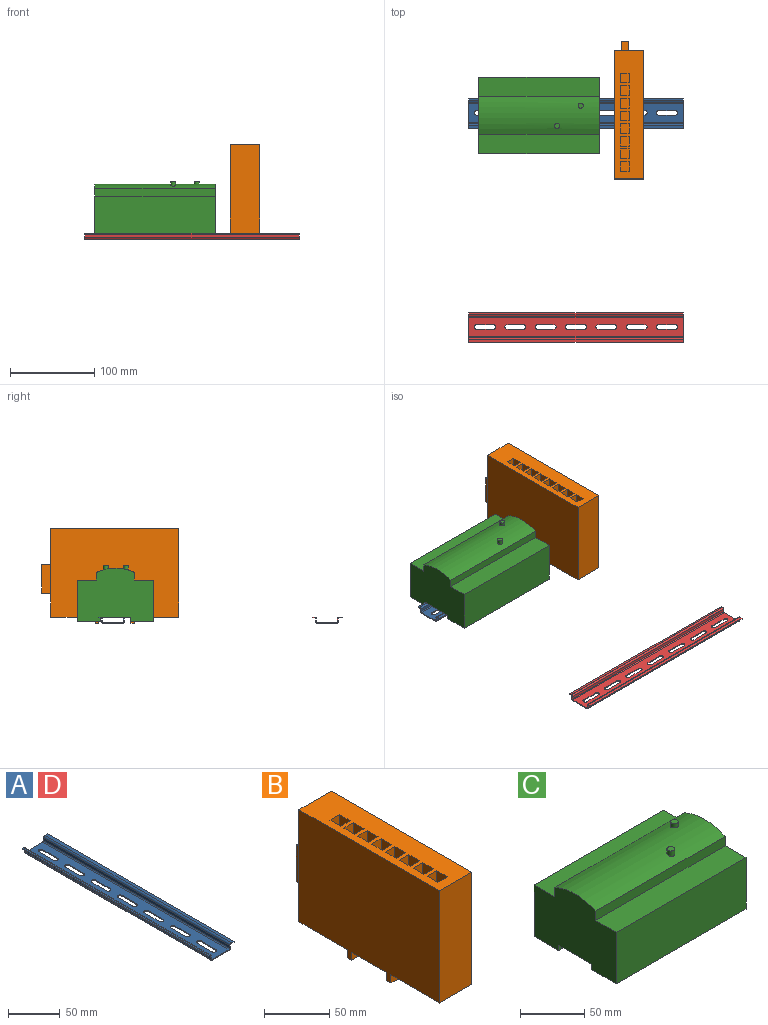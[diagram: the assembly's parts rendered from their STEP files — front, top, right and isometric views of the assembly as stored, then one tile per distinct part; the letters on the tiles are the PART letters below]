
ASSEMBLY  parts=4 mates=4
PART A: 50 faces, bbox 35x254x7.5 mm
  f0: cylinder r=1mm len=254mm, axis (0,1,0), area 399.3mm2, adj f1,f19,f20,f21
  f1: plane 254x3.5mm, normal (1,0,0), area 889mm2, adj f0,f2,f20,f21
  f2: cylinder r=2mm len=254mm, axis (0,1,0), area 797.6mm2, adj f1,f3,f20,f21
  f3: plane 254x2.19mm, normal (0,0,1), area 556.3mm2, adj f2,f4,f20,f21
  f4: plane 254x1mm, normal (-1,0,0), area 254.2mm2, adj f3,f5,f20,f21
  f5: plane 254x2.17mm, normal (0,0,-1), area 551.7mm2, adj f4,f6,f20,f21
  f6: cylinder r=1mm len=254mm, axis (0,1,0), area 399.3mm2, adj f5,f7,f20,f21
  f7: plane 254x3.5mm, normal (-1,0,0), area 889mm2, adj f6,f8,f20,f21
  f8: cylinder r=2mm len=254mm, axis (0,1,0), area 797.6mm2, adj f7,f9,f20,f21
  f9: plane 254x23mm, normal (0,0,-1), area 4973.3mm2, adj f8,f10,f20,f21,f22,f23,f24,f25
  f10: cylinder r=2mm len=254mm, axis (0,1,0), area 797.6mm2, adj f9,f11,f20,f21
  f11: plane 254x3.5mm, normal (1,0,0), area 889mm2, adj f10,f12,f20,f21
  f12: cylinder r=1mm len=254mm, axis (0,1,0), area 399.3mm2, adj f11,f13,f20,f21
  f13: plane 254x3.83mm, normal (0,0,-1), area 972.1mm2, adj f12,f14,f20,f21
  f14: plane 254x1mm, normal (1,0,0), area 254.2mm2, adj f13,f15,f20,f21
  f15: plane 254x3.81mm, normal (0,0,1), area 968.3mm2, adj f14,f16,f20,f21
  f16: cylinder r=2mm len=254mm, axis (0,1,0), area 797.6mm2, adj f15,f17,f20,f21
  f17: plane 254x3.5mm, normal (-1,0,0), area 889mm2, adj f16,f18,f20,f21
  f18: cylinder r=1mm len=254mm, axis (0,1,0), area 399.3mm2, adj f17,f19,f20,f21
  f19: plane 254x23mm, normal (0,0,1), area 4972.7mm2, adj f0,f18,f20,f21,f22,f23,f24,f25
  f20: plane 35x7.5mm, normal (0,-1,0), area 45.5mm2, adj f0,f1,f2,f3,f4,f5,f6,f7
  f21: plane 35x7.5mm, normal (0,1,0), area 45.5mm2, adj f0,f1,f2,f3,f4,f5,f6,f7
  f22: cylinder r=2.6mm len=5.2mm, axis (0,0,1), area 8.2mm2, adj f9,f19,f23,f25
  f23: plane 19.8x1mm, normal (1,0,0), area 19.8mm2, adj f9,f19,f22,f24
  f24: cylinder r=2.6mm len=5.2mm, axis (0,0,1), area 8.2mm2, adj f9,f19,f23,f25
  f25: plane 19.8x1mm, normal (-1,0,0), area 19.8mm2, adj f9,f19,f22,f24
  f26: plane 19.8x1mm, normal (-1,0,0), area 19.8mm2, adj f9,f19,f27,f29
  f27: cylinder r=2.6mm len=5.2mm, axis (0,0,1), area 8.2mm2, adj f9,f19,f26,f28
  f28: plane 19.8x1mm, normal (1,0,0), area 19.8mm2, adj f9,f19,f27,f29
  f29: cylinder r=2.6mm len=5.2mm, axis (0,0,1), area 8.2mm2, adj f9,f19,f26,f28
  f30: cylinder r=2.6mm len=5.2mm, axis (0,0,1), area 8.2mm2, adj f9,f19,f31,f33
  f31: plane 19.8x1mm, normal (1,0,0), area 19.8mm2, adj f9,f19,f30,f32
  f32: cylinder r=2.6mm len=5.2mm, axis (0,0,1), area 8.2mm2, adj f9,f19,f31,f33
  f33: plane 19.8x1mm, normal (-1,0,0), area 19.8mm2, adj f9,f19,f30,f32
  f34: cylinder r=2.6mm len=5.2mm, axis (0,0,1), area 8.2mm2, adj f9,f19,f35,f37
  f35: plane 19.8x1mm, normal (1,0,0), area 19.8mm2, adj f9,f19,f34,f36
  f36: cylinder r=2.6mm len=5.2mm, axis (0,0,1), area 8.2mm2, adj f9,f19,f35,f37
  f37: plane 19.8x1mm, normal (-1,0,0), area 19.8mm2, adj f9,f19,f34,f36
  f38: cylinder r=2.6mm len=5.2mm, axis (0,0,1), area 8.2mm2, adj f9,f19,f39,f41
  f39: plane 19.8x1mm, normal (1,0,0), area 19.8mm2, adj f9,f19,f38,f40
  f40: cylinder r=2.6mm len=5.2mm, axis (0,0,1), area 8.2mm2, adj f9,f19,f39,f41
  f41: plane 19.8x1mm, normal (-1,0,0), area 19.8mm2, adj f9,f19,f38,f40
  f42: cylinder r=2.6mm len=5.2mm, axis (0,0,1), area 8.2mm2, adj f9,f19,f43,f45
  f43: plane 19.8x1mm, normal (1,0,0), area 19.8mm2, adj f9,f19,f42,f44
  f44: cylinder r=2.6mm len=5.2mm, axis (0,0,1), area 8.2mm2, adj f9,f19,f43,f45
  f45: plane 19.8x1mm, normal (-1,0,0), area 19.8mm2, adj f9,f19,f42,f44
  f46: cylinder r=2.6mm len=5.2mm, axis (0,0,1), area 8.2mm2, adj f9,f19,f47,f49
  f47: plane 19.8x1mm, normal (1,0,0), area 19.8mm2, adj f9,f19,f46,f48
  f48: cylinder r=2.6mm len=5.2mm, axis (0,0,1), area 8.2mm2, adj f9,f19,f47,f49
  f49: plane 19.8x1mm, normal (-1,0,0), area 19.8mm2, adj f9,f19,f46,f48
PART B: 59 faces, bbox 35x163x112.5 mm
  f0: plane 152x35mm, normal (0,0,1), area 4362.7mm2, adj f5,f6,f12,f13,f19,f20,f21,f22
  f1: plane 35x7.5mm, normal (0,-1,0), area 262.5mm2, adj f2,f11,f12,f13
  f2: plane 35x4.5mm, normal (0,0,-1), area 157.5mm2, adj f1,f3,f12,f13
  f3: plane 35x7.5mm, normal (0,1,0), area 262.5mm2, adj f2,f4,f12,f13
  f4: plane 52.5x35mm, normal (0,0,-1), area 1837.5mm2, adj f3,f5,f12,f13
  f5: plane 105x35mm, normal (0,1,0), area 3363.4mm2, adj f0,f4,f12,f13,f14,f15,f16,f17
  f6: plane 105x35mm, normal (0,-1,0), area 3675mm2, adj f0,f7,f12,f13
  f7: plane 52.5x35mm, normal (0,0,-1), area 1837.5mm2, adj f6,f8,f12,f13
  f8: plane 35x7.5mm, normal (0,-1,0), area 262.5mm2, adj f7,f9,f12,f13
  f9: plane 35x4.5mm, normal (0,0,-1), area 157.5mm2, adj f8,f10,f12,f13
  f10: plane 35x7.5mm, normal (0,1,0), area 262.5mm2, adj f9,f11,f12,f13
  f11: plane 38x35mm, normal (0,0,-1), area 1330mm2, adj f1,f10,f12,f13
  f12: plane 152x112.5mm, normal (-1,0,0), area 16027.5mm2, adj f0,f1,f2,f3,f4,f5,f6,f7
  f13: plane 152x112.5mm, normal (1,0,0), area 16027.5mm2, adj f0,f1,f2,f3,f4,f5,f6,f7
  f14: plane 11x9.08mm, normal (0,0,-1), area 99.8mm2, adj f5,f15,f17,f18
  f15: plane 34.33x11mm, normal (-1,0,0), area 377.6mm2, adj f5,f14,f16,f18
  f16: plane 11x9.08mm, normal (0,0,1), area 99.8mm2, adj f5,f15,f17,f18
  f17: plane 34.33x11mm, normal (1,0,0), area 377.6mm2, adj f5,f14,f16,f18
  f18: plane 34.33x9.08mm, normal (0,1,0), area 311.6mm2, adj f14,f15,f16,f17
  f19: plane 15x11.63mm, normal (-1,0,0), area 174.5mm2, adj f0,f20,f22,f23
  f20: plane 15x10.29mm, normal (0,-1,0), area 154.3mm2, adj f0,f19,f21,f23
  f21: plane 15x11.63mm, normal (1,0,0), area 174.5mm2, adj f0,f20,f22,f23
  f22: plane 15x10.29mm, normal (0,1,0), area 154.3mm2, adj f0,f19,f21,f23
  f23: plane 11.63x10.29mm, normal (0,0,1), area 119.7mm2, adj f19,f20,f21,f22
  f24: plane 15x11.63mm, normal (-1,0,0), area 174.5mm2, adj f0,f25,f27,f28
  f25: plane 15x10.29mm, normal (0,-1,0), area 154.3mm2, adj f0,f24,f26,f28
  f26: plane 15x11.63mm, normal (1,0,0), area 174.5mm2, adj f0,f25,f27,f28
  f27: plane 15x10.29mm, normal (0,1,0), area 154.3mm2, adj f0,f24,f26,f28
  f28: plane 11.63x10.29mm, normal (0,0,1), area 119.7mm2, adj f24,f25,f26,f27
  f29: plane 15x11.63mm, normal (-1,0,0), area 174.5mm2, adj f0,f30,f32,f33
  f30: plane 15x10.29mm, normal (0,-1,0), area 154.3mm2, adj f0,f29,f31,f33
  f31: plane 15x11.63mm, normal (1,0,0), area 174.5mm2, adj f0,f30,f32,f33
  f32: plane 15x10.29mm, normal (0,1,0), area 154.3mm2, adj f0,f29,f31,f33
  f33: plane 11.63x10.29mm, normal (0,0,1), area 119.7mm2, adj f29,f30,f31,f32
  f34: plane 15x11.63mm, normal (-1,0,0), area 174.5mm2, adj f0,f35,f37,f38
  f35: plane 15x10.29mm, normal (0,-1,0), area 154.3mm2, adj f0,f34,f36,f38
  f36: plane 15x11.63mm, normal (1,0,0), area 174.5mm2, adj f0,f35,f37,f38
  f37: plane 15x10.29mm, normal (0,1,0), area 154.3mm2, adj f0,f34,f36,f38
  f38: plane 11.63x10.29mm, normal (0,0,1), area 119.7mm2, adj f34,f35,f36,f37
  f39: plane 15x11.63mm, normal (-1,0,0), area 174.5mm2, adj f0,f40,f42,f43
  f40: plane 15x10.29mm, normal (0,-1,0), area 154.3mm2, adj f0,f39,f41,f43
  f41: plane 15x11.63mm, normal (1,0,0), area 174.5mm2, adj f0,f40,f42,f43
  f42: plane 15x10.29mm, normal (0,1,0), area 154.3mm2, adj f0,f39,f41,f43
  f43: plane 11.63x10.29mm, normal (0,0,1), area 119.7mm2, adj f39,f40,f41,f42
  f44: plane 15x11.63mm, normal (-1,0,0), area 174.5mm2, adj f0,f45,f47,f48
  f45: plane 15x10.29mm, normal (0,-1,0), area 154.3mm2, adj f0,f44,f46,f48
  f46: plane 15x11.63mm, normal (1,0,0), area 174.5mm2, adj f0,f45,f47,f48
  f47: plane 15x10.29mm, normal (0,1,0), area 154.3mm2, adj f0,f44,f46,f48
  f48: plane 11.63x10.29mm, normal (0,0,1), area 119.7mm2, adj f44,f45,f46,f47
  f49: plane 15x11.63mm, normal (-1,0,0), area 174.5mm2, adj f0,f50,f52,f53
  f50: plane 15x10.29mm, normal (0,-1,0), area 154.3mm2, adj f0,f49,f51,f53
  f51: plane 15x11.63mm, normal (1,0,0), area 174.5mm2, adj f0,f50,f52,f53
  f52: plane 15x10.29mm, normal (0,1,0), area 154.3mm2, adj f0,f49,f51,f53
  f53: plane 11.63x10.29mm, normal (0,0,1), area 119.7mm2, adj f49,f50,f51,f52
  f54: plane 15x11.63mm, normal (1,0,0), area 174.5mm2, adj f0,f55,f57,f58
  f55: plane 15x10.29mm, normal (0,1,0), area 154.3mm2, adj f0,f54,f56,f58
  f56: plane 15x11.63mm, normal (-1,0,0), area 174.5mm2, adj f0,f55,f57,f58
  f57: plane 15x10.29mm, normal (0,-1,0), area 154.3mm2, adj f0,f54,f56,f58
  f58: plane 11.63x10.29mm, normal (0,0,1), area 119.7mm2, adj f54,f55,f56,f57
PART C: 18 faces, bbox 143x91x66 mm
  f0: plane 143x36mm, normal (0,0,-1), area 5148mm2, adj f1,f11,f12,f13
  f1: plane 143x5mm, normal (0,-1,0), area 715mm2, adj f0,f2,f12,f13
  f2: plane 143x27.5mm, normal (0,0,-1), area 3932.5mm2, adj f1,f3,f12,f13
  f3: plane 143x49mm, normal (0,1,0), area 7007mm2, adj f2,f4,f12,f13
  f4: plane 143x23mm, normal (0,0,1), area 3289mm2, adj f3,f5,f12,f13
  f5: plane 143x9mm, normal (0,1,0), area 1287mm2, adj f4,f6,f12,f13
  f6: cylinder r=53.12mm len=143mm, axis (1,0,0), area 6586.7mm2, adj f5,f7,f12,f13,f14,f16
  f7: plane 143x9mm, normal (0,-1,0), area 1287mm2, adj f6,f8,f12,f13
  f8: plane 143x23mm, normal (0,0,1), area 3289mm2, adj f7,f9,f12,f13
  f9: plane 143x49mm, normal (0,-1,0), area 7007mm2, adj f8,f10,f12,f13
  f10: plane 143x27.5mm, normal (0,0,-1), area 3932.5mm2, adj f9,f11,f12,f13
  f11: plane 143x5mm, normal (0,1,0), area 715mm2, adj f0,f10,f12,f13
  f12: plane 91x63mm, normal (-1,0,0), area 4835.5mm2, adj f0,f1,f2,f3,f4,f5,f6,f7
  f13: plane 91x63mm, normal (1,0,0), area 4835.5mm2, adj f0,f1,f2,f3,f4,f5,f6,f7
  f14: cylinder r=3mm len=6mm, axis (0,0,-1), area 81.2mm2, adj f6,f15
  f15: plane 6x6mm, normal (0,0,1), area 28.3mm2, adj f14
  f16: cylinder r=3mm len=6mm, axis (0,0,-1), area 85.5mm2, adj f6,f17
  f17: plane 6x6mm, normal (0,0,1), area 28.3mm2, adj f16
PART D: same geometry as A
PLACE A rot(axis=(0,0,-1),90deg) t=(4.82,1.8,-2.16)mm fixed
PLACE B t=(85.49,-0.67,5.34)mm
PLACE C t=(32.47,-1.19,0.34)mm
PLACE D rot(axis=(0,0,-1),90deg) t=(4.82,-252.2,-2.16)mm
MATE fastened D.f9 <-> A.f9  axis (0,0,-1) through (131.82,-263.7,-2.16)mm
MATE planar A.f3 <-> C.f0  axis (0,0,1) through (4.82,17.38,5.34)mm
MATE planar B.f11 <-> A.f3  axis (0,0,-1) through (67.99,-0.67,5.34)mm
MATE parallel D.f9 <-> A.f9  axis (0,0,-1) through (4.82,-252.2,-2.16)mm
